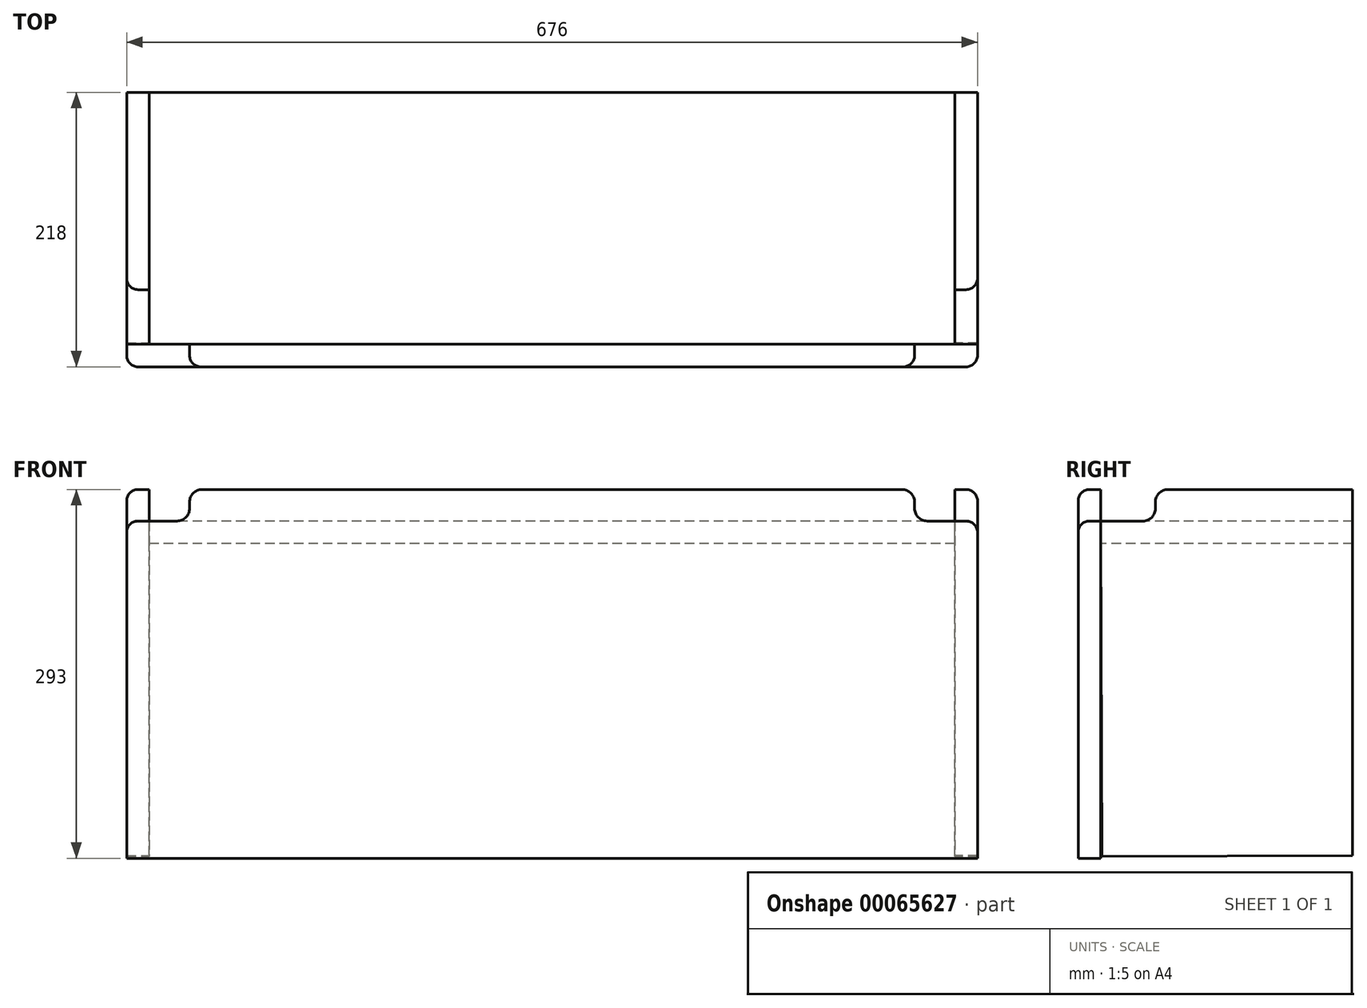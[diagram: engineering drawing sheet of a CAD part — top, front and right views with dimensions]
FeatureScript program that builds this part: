
annotation { "Feature Type Name" : "Feature", "Feature Type Description" : "" }
export const myFeature = defineFeature(function(context is Context, id is Id, definition is map)
    precondition{}
    {
        {
            var Q0;
            Q0=qCreatedBy(makeId("Top.planeOp"),FACE);
            var sketch = newSketch(context, id + "F0", { "sketchPlane" : qUnion([Q0])});
            skLineSegment(sketch, "E0", {"start": v(0, 0) * mm, "end": v(-320, 0) * mm});
            skLineSegment(sketch, "E1", {"start": v(-320, 200) * mm, "end": v(-320, 0) * mm});
            skLineSegment(sketch, "E2", {"start": v(-320, 200) * mm, "end": v(0, 200) * mm});
            skLineSegment(sketch, "E3.MirrorCS", {"start": v(320, 200) * mm, "end": v(0, 200) * mm});
            skLineSegment(sketch, "E4.MirrorCS", {"start": v(320, 200) * mm, "end": v(320, 0) * mm});
            skLineSegment(sketch, "E5.MirrorCS", {"start": v(0, 0) * mm, "end": v(320, 0) * mm});
            skSolve(sketch);
        }
        {
            var Q0;
            Q0=makeQuery(id+"F0.imprint","IMPRINT",FACE,{"disambiguationData":[TD([[makeQuery(id+"F0.imprint","IMPRINT",EDGE,{"derivedFrom":sQuery(id+"F0.wireOp",EDGE,"E0")}),-1.0]])]});
            extrude(context, id + "F1", {"entities" : qUnion([Q0]), "oppositeDirection" : true, "depth" : 18 * mm});
        }
        {
            var Q0;
            Q0=qCreatedBy(makeId("Front.planeOp"),FACE);
            var sketch = newSketch(context, id + "F2", { "sketchPlane" : qUnion([Q0])});
            skLineSegment(sketch, "E6.bottom", {"start": v(0, 25) * mm, "end": v(-288, 25) * mm});
            skLineSegment(sketch, "E6.top", {"start": v(0, -268) * mm, "end": v(-338, -268) * mm});
            skLineSegment(sketch, "E6.right", {"start": v(-338, 0) * mm, "end": v(-338, -268) * mm});
            skLineSegment(sketch, "E7.MirrorCS", {"start": v(0, -268) * mm, "end": v(338, -268) * mm});
            skLineSegment(sketch, "E8.MirrorCS", {"start": v(0, 25) * mm, "end": v(288, 25) * mm});
            skLineSegment(sketch, "E9.MirrorCS", {"start": v(338, 0) * mm, "end": v(338, -268) * mm});
            skLineSegment(sketch, "E10", {"start": v(-288, 25) * mm, "end": v(-288, 0) * mm});
            skLineSegment(sketch, "E11", {"start": v(-288, 0) * mm, "end": v(-338, 0) * mm});
            skPoint(sketch, "E12.orphan", {"position": v(-338, 25) * mm});
            skLineSegment(sketch, "E13.MirrorCS", {"start": v(288, 25) * mm, "end": v(288, 0) * mm});
            skLineSegment(sketch, "E14.MirrorCS", {"start": v(288, 0) * mm, "end": v(338, 0) * mm});
            skPoint(sketch, "E15.orphan", {"position": v(338, 25) * mm});
            skSolve(sketch);
        }
        {
            var Q0;
            Q0=makeQuery(id+"F2.imprint","IMPRINT",FACE,{"disambiguationData":[TD([[makeQuery(id+"F2.imprint","IMPRINT",EDGE,{"derivedFrom":sQuery(id+"F2.wireOp",EDGE,"E6.bottom")}),1.0]])]});
            extrude(context, id + "F3", {"entities" : qUnion([Q0]), "depth" : 18 * mm});
        }
        {
            var Q0;
            Q0=makeQuery(id+"F1.opExtrude","CAP_EDGE",EDGE,{"disambiguationData":[OSD([sQuery(id+"F0.wireOp",EDGE,"E4.MirrorCS")])],"isStart":true});
            var Q1;
            Q1=qCreatedBy(makeId("Right.planeOp"),FACE);
            cPlane(context, id + "F4", {"entities" : qUnion([Q0, Q1]), "cplaneType" : CPlaneType.LINE_ANGLE, "offset" : 0 * mm, "angle" : 0 * degree, "width" : 150 * mm, "height" : 150 * mm});
        }
        {
            var Q0;
            Q0=qCreatedBy(id+"F4.planeOp",FACE);
            var sketch = newSketch(context, id + "F5", { "sketchPlane" : qUnion([Q0])});
            skLineSegment(sketch, "E16.0", {"start": v(0, 0) * mm, "end": v(0, -268) * mm, "construction": true});
            skLineSegment(sketch, "E17.0", {"start": v(-200, -18) * mm, "end": v(0, -18) * mm, "construction": true});
            skLineSegment(sketch, "E18.0", {"start": v(18, 25) * mm, "end": v(0, 25) * mm, "construction": true});
            skLineSegment(sketch, "E19", {"start": v(-43.3, 25) * mm, "end": v(-43.3, 0) * mm});
            skLineSegment(sketch, "E20", {"start": v(-43.3, 0) * mm, "end": v(0.3, -0.56) * mm});
            skLineSegment(sketch, "E21", {"start": v(0.3, -0.56) * mm, "end": v(-0.82, -266.66) * mm});
            skLineSegment(sketch, "E22", {"start": v(-0.82, -266.66) * mm, "end": v(-200, -265.82) * mm});
            skLineSegment(sketch, "E23", {"start": v(-200, -265.82) * mm, "end": v(-200, 25) * mm});
            skLineSegment(sketch, "E24", {"start": v(-200, 25) * mm, "end": v(-43.3, 25) * mm});
            skSolve(sketch);
        }
        {
            var Q0;
            Q0=makeQuery(id+"F5.imprint","IMPRINT",FACE,{"disambiguationData":[TD([[makeQuery(id+"F5.imprint","IMPRINT",EDGE,{"derivedFrom":sQuery(id+"F5.wireOp",EDGE,"E19")}),-1.0]])]});
            extrude(context, id + "F6", {"entities" : qUnion([Q0]), "oppositeDirection" : true, "depth" : 18 * mm});
        }
        {
            var Q0;
            Q0=makeQuery(id+"F6.opExtrude","SWEPT_BODY",BODY,{"disambiguationData":[OSD([sQuery(id+"F5.wireOp",EDGE,"E19"),sQuery(id+"F5.wireOp",EDGE,"E20"),sQuery(id+"F5.wireOp",EDGE,"E21"),sQuery(id+"F5.wireOp",EDGE,"E22"),sQuery(id+"F5.wireOp",EDGE,"E23"),sQuery(id+"F5.wireOp",EDGE,"E24")])]});
            var Q1;
            Q1=qCreatedBy(makeId("Right.planeOp"),FACE);
            mirror(context, id + "F7", {"entities" : qUnion([Q0]), "mirrorPlane" : qUnion([Q1])});
        }
        {
            var Q0;
            Q0=makeQuery(id+"F6.opExtrude","SWEPT_EDGE",EDGE,{"disambiguationData":[OSD([sQuery(id+"F5.wireOp",EDGE,"E19"),sQuery(id+"F5.wireOp",EDGE,"E20")])]});
            var Q1;
            Q1=makeQuery(id+"F6.opExtrude","SWEPT_EDGE",EDGE,{"disambiguationData":[OSD([sQuery(id+"F5.wireOp",EDGE,"E19"),sQuery(id+"F5.wireOp",EDGE,"E24")])]});
            var Q2;
            Q2=makeQuery(id+"F3.opExtrude","SWEPT_EDGE",EDGE,{"disambiguationData":[OSD([sQuery(id+"F2.wireOp",EDGE,"E13.MirrorCS"),sQuery(id+"F2.wireOp",EDGE,"E14.MirrorCS")])]});
            var Q3;
            Q3=makeQuery(id+"F3.opExtrude","SWEPT_EDGE",EDGE,{"disambiguationData":[OSD([sQuery(id+"F2.wireOp",EDGE,"E6.bottom"),sQuery(id+"F2.wireOp",EDGE,"E10")])]});
            var Q4;
            Q4=makeQuery(id+"F3.opExtrude","SWEPT_EDGE",EDGE,{"disambiguationData":[OSD([sQuery(id+"F2.wireOp",EDGE,"E10"),sQuery(id+"F2.wireOp",EDGE,"E11")])]});
            var Q5;
            Q5=makeQuery(id+"F7.opPattern","COPY",EDGE,{"derivedFrom":makeQuery(id+"F6.opExtrude","SWEPT_EDGE",EDGE,{"disambiguationData":[OSD([sQuery(id+"F5.wireOp",EDGE,"E19"),sQuery(id+"F5.wireOp",EDGE,"E20")])]}),"instanceName":"1"});
            var Q6;
            Q6=makeQuery(id+"F7.opPattern","COPY",EDGE,{"derivedFrom":makeQuery(id+"F6.opExtrude","SWEPT_EDGE",EDGE,{"disambiguationData":[OSD([sQuery(id+"F5.wireOp",EDGE,"E19"),sQuery(id+"F5.wireOp",EDGE,"E24")])]}),"instanceName":"1"});
            var Q7;
            Q7=makeQuery(id+"F3.opExtrude","SWEPT_EDGE",EDGE,{"disambiguationData":[OSD([sQuery(id+"F2.wireOp",EDGE,"E8.MirrorCS"),sQuery(id+"F2.wireOp",EDGE,"E13.MirrorCS")])]});
            fillet(context, id + "F8", {"entities" : qUnion([Q0, Q1, Q2, Q3, Q4, Q5, Q6, Q7]), "radius" : 10 * mm, "tangentPropagation" : true, "allowEdgeOverflow" : false});
        }
        {
            var Q0;
            Q0=makeQuery(id+"F6.opExtrude","CAP_EDGE",EDGE,{"disambiguationData":[OSD([sQuery(id+"F5.wireOp",EDGE,"E24")])],"isStart":false});
            var Q1;
            Q1=makeQuery(id+"F3.opExtrude","SWEPT_EDGE",EDGE,{"disambiguationData":[OSD([sQuery(id+"F2.wireOp",EDGE,"E9.MirrorCS"),sQuery(id+"F2.wireOp",EDGE,"E14.MirrorCS")])]});
            var Q2;
            Q2=makeQuery(id+"F3.opExtrude","CAP_EDGE",EDGE,{"disambiguationData":[OSD([sQuery(id+"F2.wireOp",EDGE,"E6.bottom"),sQuery(id+"F2.wireOp",EDGE,"E8.MirrorCS")])],"isStart":false});
            var Q3;
            Q3=makeQuery(id+"F3.opExtrude","CAP_EDGE",EDGE,{"disambiguationData":[OSD([sQuery(id+"F2.wireOp",EDGE,"E9.MirrorCS")])],"isStart":false});
            var Q4;
            Q4=makeQuery(id+"F3.opExtrude","CAP_EDGE",EDGE,{"disambiguationData":[OSD([sQuery(id+"F2.wireOp",EDGE,"E6.right")])],"isStart":false});
            var Q5;
            Q5=makeQuery(id+"F7.opPattern","COPY",EDGE,{"derivedFrom":makeQuery(id+"F6.opExtrude","CAP_EDGE",EDGE,{"disambiguationData":[OSD([sQuery(id+"F5.wireOp",EDGE,"E24")])],"isStart":false}),"instanceName":"1"});
            var Q6;
            Q6=makeQuery(id+"F3.opExtrude","SWEPT_EDGE",EDGE,{"disambiguationData":[OSD([sQuery(id+"F2.wireOp",EDGE,"E6.right"),sQuery(id+"F2.wireOp",EDGE,"E11")])]});
            fillet(context, id + "F9", {"entities" : qUnion([Q0, Q1, Q2, Q3, Q4, Q5, Q6]), "radius" : 9 * mm, "tangentPropagation" : true, "allowEdgeOverflow" : false});
        }
    });
